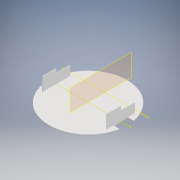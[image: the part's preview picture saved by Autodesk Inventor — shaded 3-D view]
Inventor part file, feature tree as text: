
AUTODESK INVENTOR PART (.ipt)
format: ipt  version: 2020 (Build 240168000, 168)  size: 251,392 bytes
history: native  units: mm
features: extrude x10, sketch x10, reference x10, other x6, plane x3, fillet x1, mirror x1, projected_geometry x1
ambient origin geometry x8: Origin, YZ Plane, XZ Plane, XY Plane, X Axis, Y Axis, Z Axis, Center Point
bodies: Solid1 (feature_tree)
feature tree (42):
  extrude  "Extrusion1"  Depth=1.0mm TaperAngle=0.0deg
  extrude  "Extrusion2"  Depth=2.0mm
  extrude  "Extrusion4"  Depth=32.563mm
  plane  "Work Plane1"
  plane  "Work Plane2"
  extrude  "Extrusion5"  Depth=0.5mm
  plane  "Work Plane3"
  extrude  "Extrusion6"  Depth=0.5mm
  extrude  "Extrusion7"  Depth=1.0mm
  extrude  "Extrusion8"  Depth=2.0mm
  extrude  "Extrusion13"  Depth=0.5mm TaperAngle=0.0deg
  extrude  "Extrusion14"  Depth=1.0mm
  fillet  "Fillet1"  Radius=1.0mm
  mirror  "Mirror1"
  extrude  "Extrusion15"  Depth=1.0mm TaperAngle=0.0deg
  sketch  "Sketch1"  dims[d0=150.0mm d1=1.0mm d2=0.0mm]
  sketch  "Sketch2"  dims[d3=2.0mm d4=2.0mm]
  reference  "Reference1"
  projected_geometry  "Projected Loop1"
  reference  "Reference2"
  sketch  "Sketch6"  dims[d5=1.0mm d6=0.0mm d15=32.563mm]
  sketch  "Sketch8"  dims[d16=1.0mm d18=0.5mm]
  sketch  "Sketch9"  dims[d19=2.0mm d20=0.5mm]
  sketch  "Sketch10"  dims[d21=32.563mm d22=1.0mm]
  reference  "Reference3"
  reference  "Reference4"
  reference  "Reference5"
  reference  "Reference6"
  reference  "Reference7"
  reference  "Reference8"
  reference  "Reference9"
  reference  "Reference10"
  sketch  "Sketch11"  dims[d23=0.5mm d24=2.0mm]
  sketch  "Sketch17"  dims[d25=0.5mm d26=0.5mm d27=0.0mm]
  sketch  "Sketch18"  dims[d28=-1.0mm d29=1.0mm d30=1.0mm]
  sketch  "Sketch19"  dims[d31=0.5mm d32=0.0mm d33=1.0mm d34=0.0mm d35=3.0mm d36=0.0mm d38=27.0mm d39=1.0mm d40=0.0mm d53=54.0mm d54=25.5mm d55=0.0mm d56=1.0mm d57=0.0mm d58=2.0mm d59=1.0mm d60=0.0mm d37=0.5mm]
  other  "<userpath>\Documents\Draws_Inventor\Robocup_robot\Robot_assembly.iam"
  other  "Robot_assembly.iam"
  other  "KonstrukcijaDonjiDio_v.1.2:1"
  other  "<userpath>\Documents\Draws_Inventor\Inventor_Robocup\Robot_assembly.iam"
  other  "Raspberry Pi 4 Model B:1"
  other  "PCB, RPi4ModelB_1"
